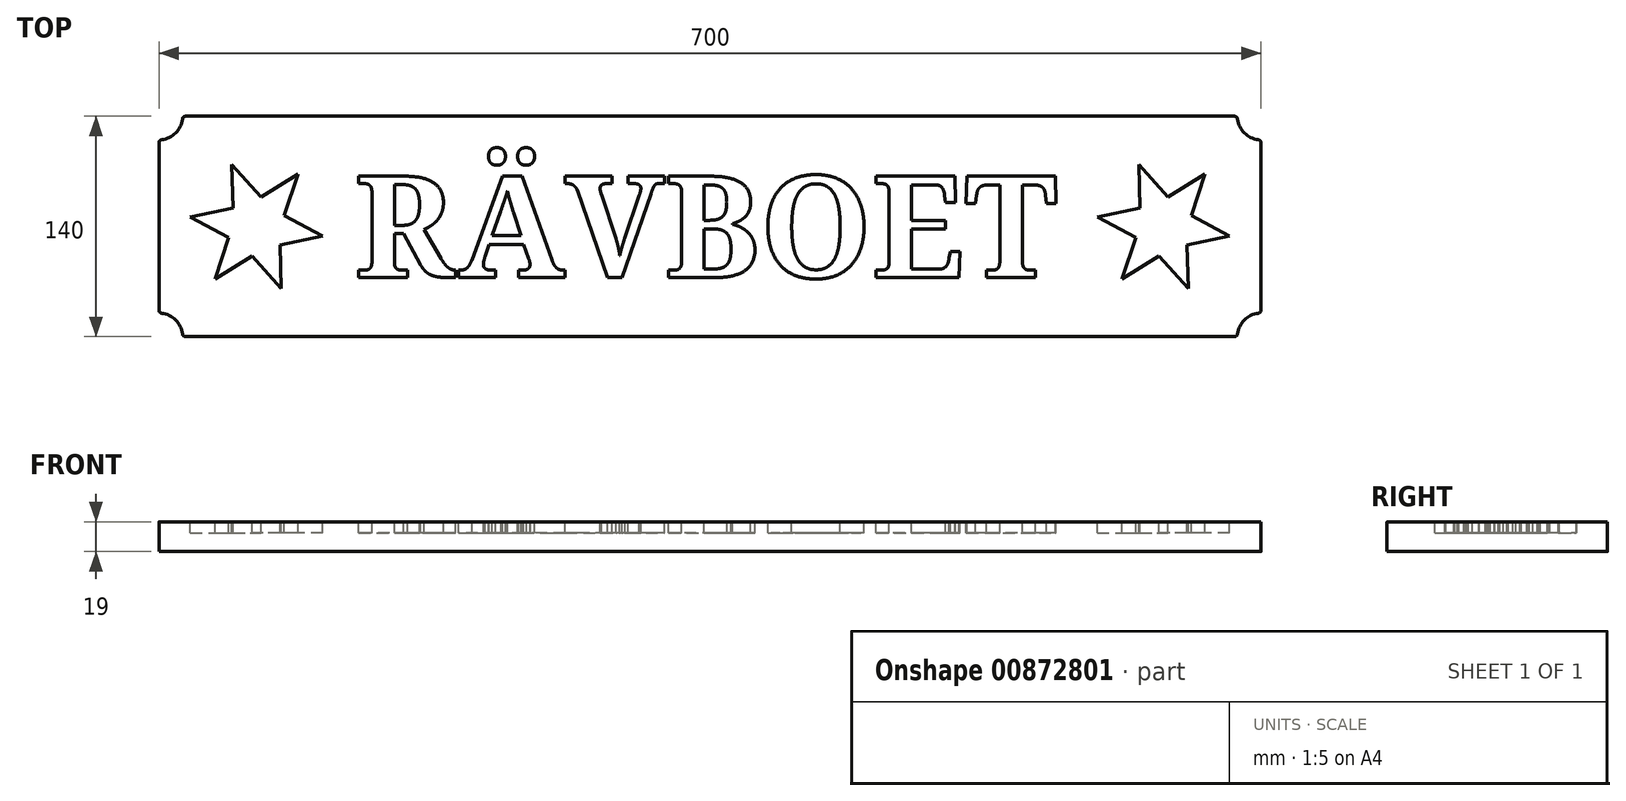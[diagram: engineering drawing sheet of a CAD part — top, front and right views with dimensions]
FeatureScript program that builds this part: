
annotation { "Feature Type Name" : "Feature", "Feature Type Description" : "" }
export const myFeature = defineFeature(function(context is Context, id is Id, definition is map)
    precondition{}
    {
        {
            var Q0;
            Q0=qCreatedBy(makeId("Top.planeOp"),FACE);
            var sketch = newSketch(context, id + "F0", { "sketchPlane" : qUnion([Q0])});
            skLineSegment(sketch, "E0.bottom", {"start": v(-333.12, 70) * mm, "end": v(0, 70) * mm});
            skLineSegment(sketch, "E0.top", {"start": v(-350, 0) * mm, "end": v(0, 0) * mm});
            skLineSegment(sketch, "E0.left", {"start": v(-350, 53.12) * mm, "end": v(-350, 0) * mm});
            skLineSegment(sketch, "E0.right", {"start": v(0, 70) * mm, "end": v(0, 0) * mm});
            skArc(sketch, "E1", {"start": v(-348.24, 55.1) * mm, "mid": v(-339.4, 59.4) * mm, "end": v(-335.1, 68.24) * mm});
            skLineSegment(sketch, "E2.MirrorCS", {"start": v(350, 0) * mm, "end": v(0, 0) * mm});
            skLineSegment(sketch, "E3.MirrorCS", {"start": v(333.12, 70) * mm, "end": v(0, 70) * mm});
            skLineSegment(sketch, "E4.MirrorCS", {"start": v(350, 53.12) * mm, "end": v(350, 0) * mm});
            skArc(sketch, "E5.MirrorC", {"start": v(348.24, 55.1) * mm, "mid": v(339.4, 59.4) * mm, "end": v(335.1, 68.24) * mm});
            skLineSegment(sketch, "E6.MirrorCS", {"start": v(0, -70) * mm, "end": v(0, 0) * mm});
            skArc(sketch, "E7.MirrorC", {"start": v(-348.24, -55.1) * mm, "mid": v(-339.4, -59.4) * mm, "end": v(-335.1, -68.24) * mm});
            skLineSegment(sketch, "E8.MirrorCS", {"start": v(-333.12, -70) * mm, "end": v(0, -70) * mm});
            skLineSegment(sketch, "E9.MirrorCS", {"start": v(-350, -53.12) * mm, "end": v(-350, 0) * mm});
            skLineSegment(sketch, "E10.MirrorCS", {"start": v(350, -53.12) * mm, "end": v(350, 0) * mm});
            skLineSegment(sketch, "E11.MirrorCS", {"start": v(333.12, -70) * mm, "end": v(0, -70) * mm});
            skArc(sketch, "E12.MirrorC", {"start": v(348.24, -55.1) * mm, "mid": v(339.4, -59.4) * mm, "end": v(335.1, -68.24) * mm});
            skPoint(sketch, "E13.visualSharp", {"position": v(-335, 70) * mm});
            skArc(sketch, "E13.filletArc", {"start": v(-333.12, 70) * mm, "mid": v(-334.45, 69.5) * mm, "end": v(-335.1, 68.24) * mm});
            skPoint(sketch, "E14.visualSharp", {"position": v(-350, 55) * mm});
            skArc(sketch, "E14.filletArc", {"start": v(-348.24, 55.1) * mm, "mid": v(-349.5, 54.45) * mm, "end": v(-350, 53.12) * mm});
            skPoint(sketch, "E15.visualSharp", {"position": v(-350, -55) * mm});
            skArc(sketch, "E15.filletArc", {"start": v(-350, -53.12) * mm, "mid": v(-349.5, -54.45) * mm, "end": v(-348.24, -55.1) * mm});
            skPoint(sketch, "E16.visualSharp", {"position": v(-335, -70) * mm});
            skArc(sketch, "E16.filletArc", {"start": v(-335.1, -68.24) * mm, "mid": v(-334.45, -69.5) * mm, "end": v(-333.12, -70) * mm});
            skPoint(sketch, "E17.visualSharp", {"position": v(335, 70) * mm});
            skArc(sketch, "E17.filletArc", {"start": v(335.1, 68.24) * mm, "mid": v(334.45, 69.5) * mm, "end": v(333.12, 70) * mm});
            skPoint(sketch, "E18.visualSharp", {"position": v(350, 55) * mm});
            skArc(sketch, "E18.filletArc", {"start": v(350, 53.12) * mm, "mid": v(349.5, 54.45) * mm, "end": v(348.24, 55.1) * mm});
            skPoint(sketch, "E19.visualSharp", {"position": v(350, -55) * mm});
            skArc(sketch, "E19.filletArc", {"start": v(348.24, -55.1) * mm, "mid": v(349.5, -54.45) * mm, "end": v(350, -53.12) * mm});
            skPoint(sketch, "E20.visualSharp", {"position": v(335, -70) * mm});
            skArc(sketch, "E20.filletArc", {"start": v(333.12, -70) * mm, "mid": v(334.45, -69.5) * mm, "end": v(335.1, -68.24) * mm});
            skSolve(sketch);
        }
        {
            var Q0;
            Q0=qSketchRegion(id+"F0",true);
            extrude(context, id + "F1", {"entities" : qUnion([Q0]), "depth" : 19 * mm, "offsetDistance" : 25 * mm});
        }
        {
            var Q0;
            Q0=makeQuery(id+"F1.opExtrude","CAP_FACE",FACE,{"disambiguationData":[OSD([sQuery(id+"F0.wireOp",EDGE,"E0.bottom"),sQuery(id+"F0.wireOp",EDGE,"E0.left"),sQuery(id+"F0.wireOp",EDGE,"E1"),sQuery(id+"F0.wireOp",EDGE,"E3.MirrorCS"),sQuery(id+"F0.wireOp",EDGE,"E4.MirrorCS"),sQuery(id+"F0.wireOp",EDGE,"E5.MirrorC"),sQuery(id+"F0.wireOp",EDGE,"E7.MirrorC"),sQuery(id+"F0.wireOp",EDGE,"E8.MirrorCS"),sQuery(id+"F0.wireOp",EDGE,"E9.MirrorCS"),sQuery(id+"F0.wireOp",EDGE,"E10.MirrorCS"),sQuery(id+"F0.wireOp",EDGE,"E11.MirrorCS"),sQuery(id+"F0.wireOp",EDGE,"E12.MirrorC")])],"isStart":false});
            var sketch = newSketch(context, id + "F2", { "sketchPlane" : qUnion([Q0])});
            skPoint(sketch, "E21.0.midPoint", {"position": v(-259.12, -22.82) * mm});
            skLineSegment(sketch, "E22", {"start": v(-303.7, 39.5) * mm, "end": v(-302.89, 11.76) * mm});
            skLineSegment(sketch, "E23", {"start": v(-303.7, 39.5) * mm, "end": v(-285.26, 18.78) * mm});
            skLineSegment(sketch, "E24", {"start": v(-330.05, 6.14) * mm, "end": v(-305.63, -7.01) * mm});
            skLineSegment(sketch, "E25", {"start": v(-330.05, 6.14) * mm, "end": v(-302.89, 11.76) * mm});
            skLineSegment(sketch, "E26", {"start": v(-272.3, -39.5) * mm, "end": v(-273.11, -11.76) * mm});
            skLineSegment(sketch, "E27", {"start": v(-272.3, -39.5) * mm, "end": v(-290.74, -18.78) * mm});
            skLineSegment(sketch, "E28", {"start": v(-314.35, -33.35) * mm, "end": v(-290.74, -18.78) * mm});
            skLineSegment(sketch, "E29", {"start": v(-314.35, -33.35) * mm, "end": v(-305.63, -7.01) * mm});
            skLineSegment(sketch, "E30", {"start": v(-261.65, 33.35) * mm, "end": v(-285.26, 18.78) * mm});
            skLineSegment(sketch, "E31", {"start": v(-261.65, 33.35) * mm, "end": v(-270.37, 7.01) * mm});
            skLineSegment(sketch, "E32", {"start": v(-245.95, -6.14) * mm, "end": v(-270.37, 7.01) * mm});
            skLineSegment(sketch, "E33", {"start": v(-245.95, -6.14) * mm, "end": v(-273.11, -11.76) * mm});
            skPoint(sketch, "E34.center.orphan", {"position": v(-288, 0) * mm});
            skCircle(sketch, "E35", {"center": v(-288, 0) * mm, "radius": 18.98 * mm, "construction": true});
            skCircle(sketch, "E36", {"center": v(-288, 0) * mm, "radius": 42.5 * mm, "construction": true});
            skPoint(sketch, "E37.0.midPoint", {"position": v(316.88, -22.82) * mm});
            skLineSegment(sketch, "E38", {"start": v(272.3, 39.5) * mm, "end": v(273.11, 11.76) * mm});
            skLineSegment(sketch, "E39", {"start": v(272.3, 39.5) * mm, "end": v(290.74, 18.78) * mm});
            skLineSegment(sketch, "E40", {"start": v(245.95, 6.14) * mm, "end": v(270.37, -7.01) * mm});
            skLineSegment(sketch, "E41", {"start": v(245.95, 6.14) * mm, "end": v(273.11, 11.76) * mm});
            skLineSegment(sketch, "E42", {"start": v(303.7, -39.5) * mm, "end": v(302.89, -11.76) * mm});
            skLineSegment(sketch, "E43", {"start": v(303.7, -39.5) * mm, "end": v(285.26, -18.78) * mm});
            skLineSegment(sketch, "E44", {"start": v(261.65, -33.35) * mm, "end": v(285.26, -18.78) * mm});
            skLineSegment(sketch, "E45", {"start": v(261.65, -33.35) * mm, "end": v(270.37, -7.01) * mm});
            skLineSegment(sketch, "E46", {"start": v(314.35, 33.35) * mm, "end": v(290.74, 18.78) * mm});
            skLineSegment(sketch, "E47", {"start": v(314.35, 33.35) * mm, "end": v(305.63, 7.01) * mm});
            skLineSegment(sketch, "E48", {"start": v(330.05, -6.14) * mm, "end": v(305.63, 7.01) * mm});
            skLineSegment(sketch, "E49", {"start": v(330.05, -6.14) * mm, "end": v(302.89, -11.76) * mm});
            skPoint(sketch, "E50.center.orphan", {"position": v(288, 0) * mm});
            skCircle(sketch, "E51", {"center": v(288, 0) * mm, "radius": 18.98 * mm, "construction": true});
            skCircle(sketch, "E52", {"center": v(288, 0) * mm, "radius": 42.5 * mm, "construction": true});
            skText(sketch, "E53", { "text": "RÄVBOET", "fontName": "NotoSerif-Bold.ttf"});
            const initialGuessF2  = {"E53": [-0.22565, -0.0325, 1, 0, 0.065]};
            skSetInitialGuess(sketch, initialGuessF2);
            skSolve(sketch);
        }
        {
            var Q0;
            Q0=qSketchRegion(id+"F2",true);
            extrude(context, id + "F3", {"entities" : qUnion([Q0]), "operationType" : NewBodyOperationType.REMOVE, "oppositeDirection" : true, "depth" : 7 * mm, "offsetDistance" : 25 * mm});
        }
    });
